FCSTD DOCUMENT  (FreeCAD 0.18R16268 (Git))
Label: Crankshaft
License: All rights reserved
LicenseURL: http://en.wikipedia.org/wiki/All_rights_reserved
objects: Sketcher::SketchObject×11, PartDesign::CoordinateSystem×9, App::DocumentObjectGroup×1, App::Part×1
note: 20 computed .brp shape members not serialized (recipe doc carries the construction recipe); baked Part::Feature solids carry a one-line shape summary decoded from their .brp

FEATURE [App::DocumentObjectGroup] Constraints
FEATURE [PartDesign::CoordinateSystem] LCS_0
  AttacherType = Attacher::AttachEngine3D
FEATURE [Sketcher::SketchObject] Sketch_arrow
  MapMode = 3
  Placement = pos=(0,0,0) rot=(1,0,0;1.5708rad)
  Support = -> [LCS_0]
  sketch-geometry (3):
    g0: LineSegment StartX=0 StartY=0 StartZ=0 EndX=0 EndY=75 EndZ=0
    g1: LineSegment StartX=0 StartY=75 StartZ=0 EndX=7.5 EndY=62.0096 EndZ=0
    g2: LineSegment StartX=0 StartY=75 StartZ=0 EndX=-7.5 EndY=62.0096 EndZ=0
  constraints (8):
    c: Coincident(g0,g-1)
    c: Vertical(g0)
    c: Coincident(g1,g0)
    c: Coincident(g2,g0)
    c: Symmetric(g2,g1,g-2)
    c: Angle(g2,g1) = 1.0472
    c: DistanceY(g0,g0) = 75
    c: Distance(g1) = 15
FEATURE [Sketcher::SketchObject] Sketch_pos_cylindres
  MapMode = 4
  Placement = pos=(0,0,0) rot=(0.57735,0.57735,0.57735;2.0944rad)
  Support = -> [LCS_0]
  sketch-geometry (5):
    g0: LineSegment StartX=0 StartY=0 StartZ=0 EndX=50 EndY=0 EndZ=0
    g1: LineSegment StartX=50 StartY=0 StartZ=0 EndX=100 EndY=0 EndZ=0
    g2: LineSegment StartX=100 StartY=0 StartZ=0 EndX=160 EndY=0 EndZ=0
    g3: LineSegment StartX=160 StartY=0 StartZ=0 EndX=210 EndY=0 EndZ=0
    g4: LineSegment StartX=210 StartY=0 StartZ=0 EndX=260 EndY=0 EndZ=0
  constraints (15):
    c: Coincident(g0,g-1)
    c: PointOnObject(g0,g-1)
    c: Coincident(g1,g0)
    c: Horizontal(g1)
    c: Coincident(g2,g1)
    c: Horizontal(g2)
    c: Coincident(g3,g2)
    c: Horizontal(g3)
    c: Coincident(g4,g3)
    c: Horizontal(g4)
    c: DistanceX(g4,g4) = 50
    c: DistanceX(g2,g2) = 60
    c: DistanceX(g1,g1) = 50
    c: DistanceX(g0,g0) = 50
    c: Equal(g1,g3)
FEATURE [Sketcher::SketchObject] Sketch_travel
  MapMode = 3
  Placement = pos=(0,0,0) rot=(1,0,0;1.5708rad)
  Support = -> [LCS_0]
  sketch-geometry (1):
    g0: Circle CenterX=0 CenterY=0 CenterZ=0 NormalX=0 NormalY=0 NormalZ=1 AngleXU=0 Radius=40
  constraints (2):
    c: Coincident(g0,g-1)
    c: Diameter(g0) = 80
FEATURE [Sketcher::SketchObject] Sketch_clocking1
  ExternalGeometry = -> [Sketch_travel]
  MapMode = 3
  Placement = pos=(0,0,0) rot=(1,0,0;1.5708rad)
  Support = -> [LCS_0]
  sketch-geometry (1):
    g0: LineSegment StartX=0 StartY=0 StartZ=0 EndX=-28.2843 EndY=28.2843 EndZ=0
  constraints (3):
    c: Coincident(g0,g-1)
    c: PointOnObject(g0,g-3)
    c: Angle(g-2,g0) = 0.785398
FEATURE [Sketcher::SketchObject] Sketch_clocking2
  ExternalGeometry = -> [Sketch_travel]
  MapMode = 3
  Placement = pos=(0,0,0) rot=(1,0,0;1.5708rad)
  Support = -> [LCS_0]
  sketch-geometry (1):
    g0: LineSegment StartX=0 StartY=0 StartZ=0 EndX=28.2843 EndY=28.2843 EndZ=0
  constraints (3):
    c: Coincident(g0,g-1)
    c: PointOnObject(g0,g-3)
    c: Angle(g-2,g0) = -0.785398
FEATURE [Sketcher::SketchObject] Sketch_clocking3
  ExternalGeometry = -> [Sketch_travel]
  MapMode = 3
  Placement = pos=(0,0,0) rot=(1,0,0;1.5708rad)
  Support = -> [LCS_0]
  sketch-geometry (1):
    g0: LineSegment StartX=0 StartY=0 StartZ=0 EndX=28.2843 EndY=-28.2843 EndZ=0
  constraints (3):
    c: Coincident(g0,g-1)
    c: PointOnObject(g0,g-3)
    c: Angle(g-2,g0) = 3.92699
FEATURE [Sketcher::SketchObject] Sketch_clocking4
  ExternalGeometry = -> [Sketch_travel]
  MapMode = 3
  Placement = pos=(0,0,0) rot=(1,0,0;1.5708rad)
  Support = -> [LCS_0]
  sketch-geometry (1):
    g0: LineSegment StartX=0 StartY=0 StartZ=0 EndX=-28.2843 EndY=-28.2843 EndZ=0
  constraints (3):
    c: Coincident(g0,g-1)
    c: PointOnObject(g0,g-3)
    c: Angle(g-2,g0) = 2.35619
FEATURE [PartDesign::CoordinateSystem] LCS_clocking1
  AttacherType = Attacher::AttachEngine3D
  AttachmentOffset = pos=(0,0,0) rot=(1,0,0;3.14159rad)
  MapMode = 49
  Placement = pos=(-28.2843,6.3e-15,28.2843) rot=(0,1,0;0.785398rad)
  Support = -> [Sketch_clocking1]
FEATURE [PartDesign::CoordinateSystem] LCS_clocking2
  AttacherType = Attacher::AttachEngine3D
  AttachmentOffset = pos=(0,0,0) rot=(1,0,0;3.14159rad)
  MapMode = 49
  Placement = pos=(28.2843,6.3e-15,28.2843) rot=(0.382683,0,-0.92388;3.14159rad)
  Support = -> [Sketch_clocking2]
FEATURE [PartDesign::CoordinateSystem] LCS_clocking3
  AttacherType = Attacher::AttachEngine3D
  AttachmentOffset = pos=(0,0,0) rot=(1,0,0;3.14159rad)
  MapMode = 49
  Placement = pos=(28.2843,-6.3e-15,-28.2843) rot=(-0.382683,0,-0.92388;3.14159rad)
  Support = -> [Sketch_clocking3]
FEATURE [PartDesign::CoordinateSystem] LCS_clocking4
  AttacherType = Attacher::AttachEngine3D
  AttachmentOffset = pos=(0,0,0) rot=(1,0,0;3.14159rad)
  MapMode = 49
  Placement = pos=(-28.2843,-6.3e-15,-28.2843) rot=(0,-1,0;0.785398rad)
  Support = -> [Sketch_clocking4]
FEATURE [PartDesign::CoordinateSystem] LCS_cylindre1
  AttacherType = Attacher::AttachEngine3D
  MapMode = 1
  Placement = pos=(0,50,0) rot=(0,0,1;0rad)
  Support = -> [Sketch_pos_cylindres]
FEATURE [PartDesign::CoordinateSystem] LCS_cylindre2
  AttacherType = Attacher::AttachEngine3D
  MapMode = 1
  Placement = pos=(0,100,0) rot=(0,0,1;0rad)
  Support = -> [Sketch_pos_cylindres]
FEATURE [PartDesign::CoordinateSystem] LCS_cylindre3
  AttacherType = Attacher::AttachEngine3D
  MapMode = 1
  Placement = pos=(0,160,0) rot=(0,0,1;0rad)
  Support = -> [Sketch_pos_cylindres]
FEATURE [PartDesign::CoordinateSystem] LCS_cylindre4
  AttacherType = Attacher::AttachEngine3D
  MapMode = 1
  Placement = pos=(0,210,0) rot=(0,0,1;0rad)
  Support = -> [Sketch_pos_cylindres]
FEATURE [Sketcher::SketchObject] Sketch_1
  ExternalGeometry = -> [Sketch_clocking1]
  MapMode = 3
  Placement = pos=(0,50,0) rot=(1,0,0;1.5708rad)
  Support = -> [LCS_cylindre1]
  sketch-geometry (1):
    g0: Circle CenterX=-28.2843 CenterY=28.2843 CenterZ=0 NormalX=0 NormalY=0 NormalZ=1 AngleXU=0 Radius=15
  constraints (2):
    c: Coincident(g0,g-3)
    c: Diameter(g0) = 30
FEATURE [Sketcher::SketchObject] Sketch_2
  ExternalGeometry = -> [Sketch_clocking2]
  MapMode = 3
  Placement = pos=(0,100,0) rot=(1,0,0;1.5708rad)
  Support = -> [LCS_cylindre2]
  sketch-geometry (1):
    g0: Circle CenterX=28.2843 CenterY=28.2843 CenterZ=0 NormalX=0 NormalY=0 NormalZ=1 AngleXU=0 Radius=15
  constraints (2):
    c: Coincident(g0,g-3)
    c: Diameter(g0) = 30
FEATURE [Sketcher::SketchObject] Sketch_3
  ExternalGeometry = -> [Sketch_clocking3]
  MapMode = 3
  Placement = pos=(0,160,0) rot=(1,0,0;1.5708rad)
  Support = -> [LCS_cylindre3]
  sketch-geometry (1):
    g0: Circle CenterX=28.2843 CenterY=-28.2843 CenterZ=0 NormalX=0 NormalY=0 NormalZ=1 AngleXU=0 Radius=15
  constraints (2):
    c: Coincident(g0,g-3)
    c: Diameter(g0) = 30
FEATURE [Sketcher::SketchObject] Sketch_4
  ExternalGeometry = -> [Sketch_clocking4]
  MapMode = 3
  Placement = pos=(0,210,0) rot=(1,0,0;1.5708rad)
  Support = -> [LCS_cylindre4]
  sketch-geometry (1):
    g0: Circle CenterX=-28.2843 CenterY=-28.2843 CenterZ=0 NormalX=0 NormalY=0 NormalZ=1 AngleXU=0 Radius=15
  constraints (2):
    c: Coincident(g0,g-3)
    c: Diameter(g0) = 30
FEATURE [App::Part] Model
  Group = -> [Constraints,LCS_0,Sketch_arrow,Sketch_pos_cylindres,Sketch_travel,Sketch_clocking1,Sketch_clocking2,Sketch_clocking3,Sketch_clocking4,LCS_clocking1,LCS_clocking2,LCS_clocking3,LCS_clocking4,LCS_cylindre1,LCS_cylindre2,LCS_cylindre3,LCS_cylindre4,Sketch_1,Sketch_2,Sketch_3,Sketch_4]
  Origin = -> Origin
